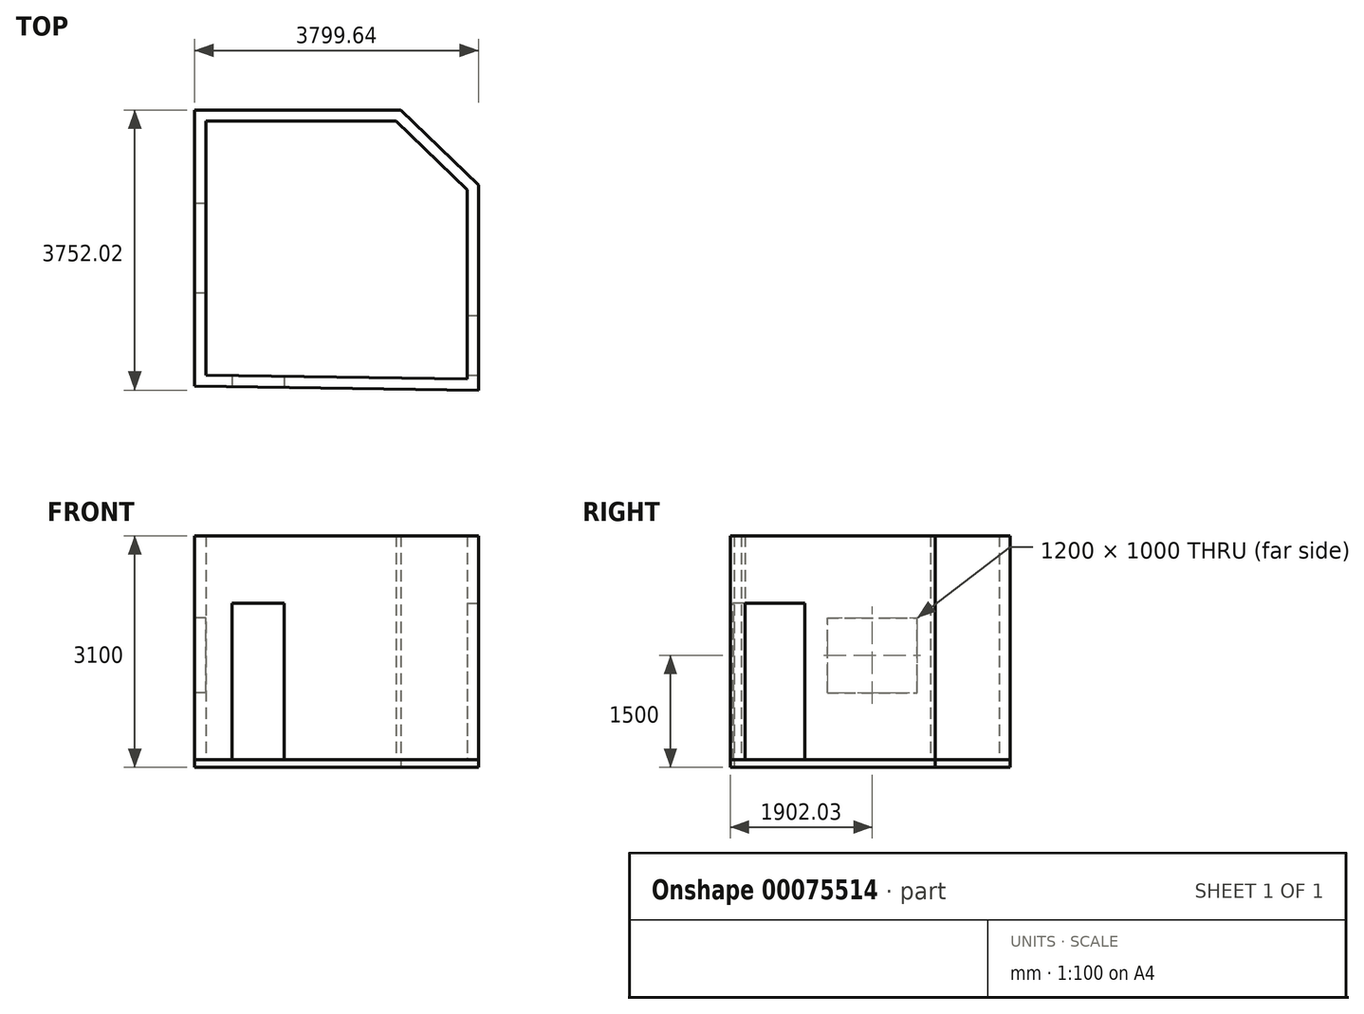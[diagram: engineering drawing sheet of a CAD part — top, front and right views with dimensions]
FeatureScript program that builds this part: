
annotation { "Feature Type Name" : "Feature", "Feature Type Description" : "" }
export const myFeature = defineFeature(function(context is Context, id is Id, definition is map)
    precondition{}
    {
        {
            var Q0;
            Q0=qCreatedBy(makeId("Top.planeOp"),FACE);
            var sketch = newSketch(context, id + "F0", { "sketchPlane" : qUnion([Q0])});
            skLineSegment(sketch, "E0.0", {"start": v(609.77, 1822.05) * mm, "end": v(1648.72, 816.8) * mm});
            skLineSegment(sketch, "E0.1", {"start": v(-2150.92, 1822.05) * mm, "end": v(609.77, 1822.05) * mm});
            skLineSegment(sketch, "E0.2", {"start": v(1648.72, 816.8) * mm, "end": v(1648.72, -1929.97) * mm});
            skLineSegment(sketch, "E0.3", {"start": v(1648.72, -1929.97) * mm, "end": v(-2150.92, -1875.82) * mm});
            skLineSegment(sketch, "E0.4", {"start": v(-2150.92, -1875.82) * mm, "end": v(-2150.92, 1822.05) * mm});
            skSolve(sketch);
        }
        {
            var Q0;
            Q0 = qSketchRegion(id + "F0", true);
            extrude(context, id + "F1", {"entities" : qUnion([Q0]), "depth" : 100 * mm});
        }
        {
            var Q0;
            Q0=makeQuery(id+"F1.opExtrude","CAP_FACE",FACE,{"disambiguationData":[OSD([sQuery(id+"F0.wireOp",EDGE,"E0.0"),sQuery(id+"F0.wireOp",EDGE,"E0.1"),sQuery(id+"F0.wireOp",EDGE,"E0.2"),sQuery(id+"F0.wireOp",EDGE,"E0.3"),sQuery(id+"F0.wireOp",EDGE,"E0.4")])],"isStart":false});
            var sketch = newSketch(context, id + "F2", { "sketchPlane" : qUnion([Q0])});
            skLineSegment(sketch, "E1", {"start": v(-2150.92, 1822.05) * mm, "end": v(609.77, 1822.05) * mm});
            skLineSegment(sketch, "E2", {"start": v(609.77, 1822.05) * mm, "end": v(1648.72, 816.8) * mm});
            skLineSegment(sketch, "E3", {"start": v(1648.72, 816.8) * mm, "end": v(1648.72, -1929.97) * mm});
            skLineSegment(sketch, "E4", {"start": v(1648.72, -1929.97) * mm, "end": v(-2150.92, -1875.82) * mm});
            skLineSegment(sketch, "E5", {"start": v(-2150.92, -1875.82) * mm, "end": v(-2150.92, 1822.05) * mm});
            skLineSegment(sketch, "E6.0", {"start": v(-2000.92, 1672.05) * mm, "end": v(549.08, 1672.05) * mm});
            skLineSegment(sketch, "E6.1", {"start": v(-2000.92, -1727.95) * mm, "end": v(-2000.92, 1672.05) * mm});
            skLineSegment(sketch, "E6.2", {"start": v(549.08, 1672.05) * mm, "end": v(1498.72, 753.22) * mm});
            skLineSegment(sketch, "E6.3", {"start": v(1498.72, 753.22) * mm, "end": v(1498.72, -1777.82) * mm});
            skLineSegment(sketch, "E6.4", {"start": v(1498.72, -1777.82) * mm, "end": v(-2000.92, -1727.95) * mm});
            skSolve(sketch);
        }
        {
            var Q0;
            Q0 = qSketchRegion(id + "F2", true);
            extrude(context, id + "F3", {"entities" : qUnion([Q0]), "depth" : 3000 * mm});
        }
        {
            var Q0;
            Q0=makeQuery(id+"F3.opExtrude","SWEPT_FACE",FACE,{"disambiguationData":[OSD([sQuery(id+"F2.wireOp",EDGE,"E4")])]});
            var sketch = newSketch(context, id + "F4", { "sketchPlane" : qUnion([Q0])});
            skLineSegment(sketch, "E7.bottom", {"start": v(-1623.97, 100) * mm, "end": v(-923.97, 100) * mm});
            skLineSegment(sketch, "E7.top", {"start": v(-1623.97, 2200) * mm, "end": v(-923.97, 2200) * mm});
            skLineSegment(sketch, "E7.left", {"start": v(-1623.97, 100) * mm, "end": v(-1623.97, 2200) * mm});
            skLineSegment(sketch, "E7.right", {"start": v(-923.97, 100) * mm, "end": v(-923.97, 2200) * mm});
            skSolve(sketch);
        }
        {
            var Q0;
            Q0 = qSketchRegion(id + "F4", true);
            extrude(context, id + "F5", {"entities" : qUnion([Q0]), "operationType" : NewBodyOperationType.REMOVE, "endBound" : BoundingType.UP_TO_NEXT, "oppositeDirection" : true, "depth" : 25 * mm});
        }
        {
            var Q0;
            Q0=makeQuery(id+"F3.opExtrude","SWEPT_FACE",FACE,{"disambiguationData":[OSD([sQuery(id+"F2.wireOp",EDGE,"E3")])]});
            var sketch = newSketch(context, id + "F6", { "sketchPlane" : qUnion([Q0])});
            skLineSegment(sketch, "E8.bottom", {"start": v(-1729.97, 100) * mm, "end": v(-929.97, 100) * mm});
            skLineSegment(sketch, "E8.top", {"start": v(-1729.97, 2200) * mm, "end": v(-929.97, 2200) * mm});
            skLineSegment(sketch, "E8.left", {"start": v(-1729.97, 100) * mm, "end": v(-1729.97, 2200) * mm});
            skLineSegment(sketch, "E8.right", {"start": v(-929.97, 100) * mm, "end": v(-929.97, 2200) * mm});
            skSolve(sketch);
        }
        {
            var Q0;
            Q0 = qSketchRegion(id + "F6", true);
            extrude(context, id + "F7", {"entities" : qUnion([Q0]), "operationType" : NewBodyOperationType.REMOVE, "endBound" : BoundingType.UP_TO_NEXT, "oppositeDirection" : true, "depth" : 25 * mm});
        }
        {
            var Q0;
            Q0=makeQuery(id+"F3.opExtrude","SWEPT_FACE",FACE,{"disambiguationData":[OSD([sQuery(id+"F2.wireOp",EDGE,"E5")])]});
            var sketch = newSketch(context, id + "F8", { "sketchPlane" : qUnion([Q0])});
            skLineSegment(sketch, "E9.bottom", {"start": v(-572.05, 2000) * mm, "end": v(627.95, 2000) * mm});
            skLineSegment(sketch, "E9.top", {"start": v(-572.05, 1000) * mm, "end": v(627.95, 1000) * mm});
            skLineSegment(sketch, "E9.left", {"start": v(-572.05, 2000) * mm, "end": v(-572.05, 1000) * mm});
            skLineSegment(sketch, "E9.right", {"start": v(627.95, 2000) * mm, "end": v(627.95, 1000) * mm});
            skSolve(sketch);
        }
        {
            var Q0;
            Q0 = qSketchRegion(id + "F8", true);
            extrude(context, id + "F9", {"entities" : qUnion([Q0]), "operationType" : NewBodyOperationType.REMOVE, "endBound" : BoundingType.UP_TO_NEXT, "oppositeDirection" : true, "depth" : 25 * mm});
        }
    });
